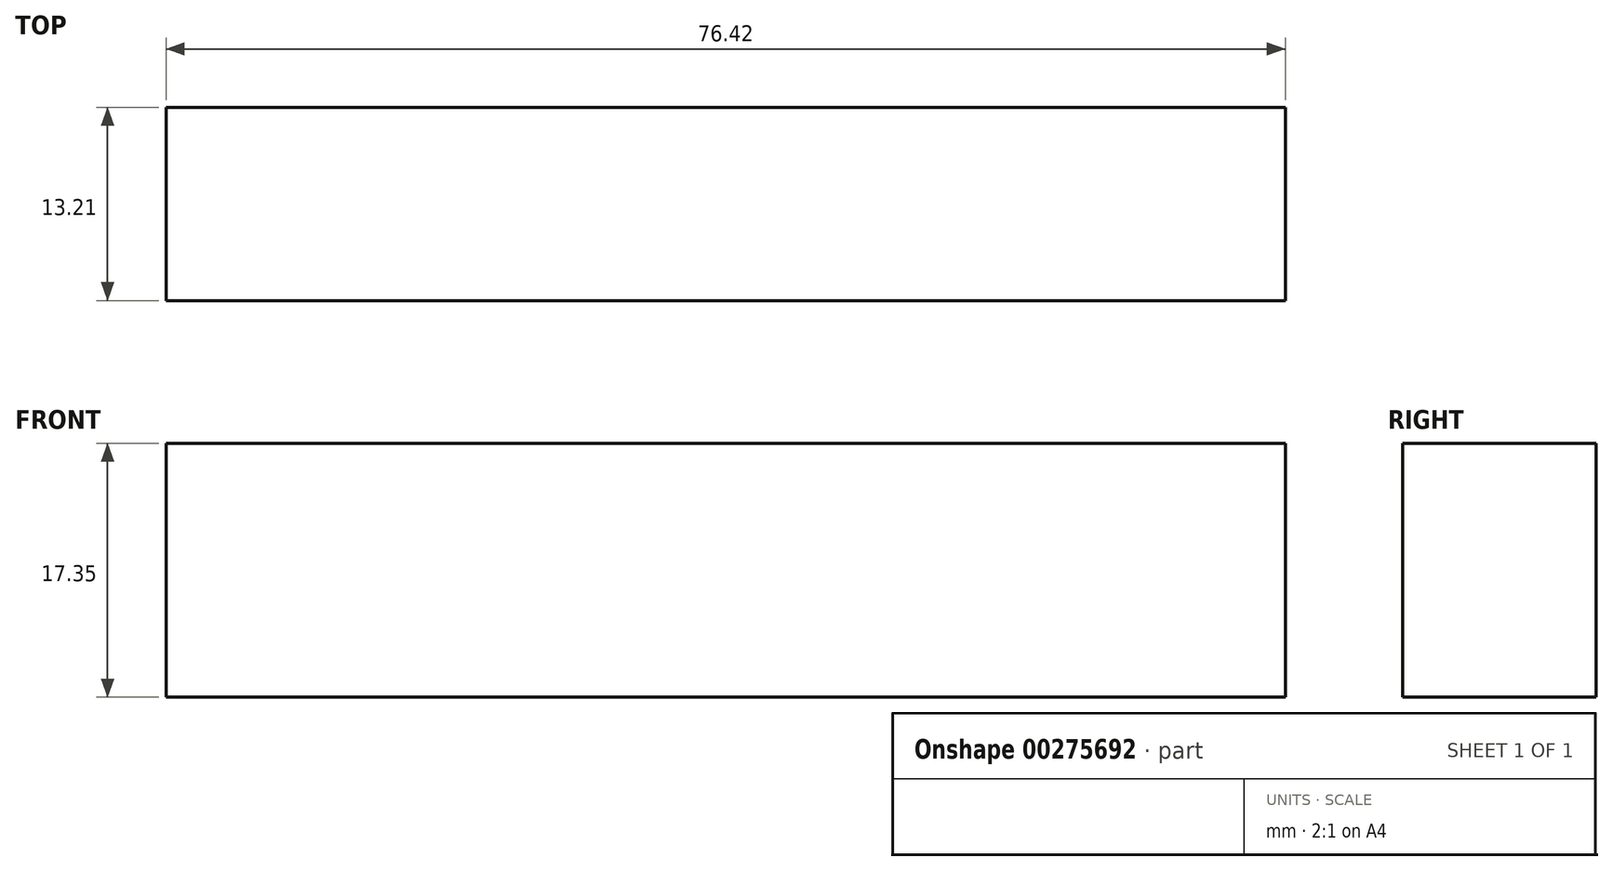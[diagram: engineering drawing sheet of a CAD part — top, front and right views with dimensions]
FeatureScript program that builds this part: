
annotation { "Feature Type Name" : "Feature", "Feature Type Description" : "" }
export const myFeature = defineFeature(function(context is Context, id is Id, definition is map)
    precondition{}
    {
        {
            var Q0;
            Q0=qCreatedBy(makeId("Front.planeOp"),FACE);
            var sketch = newSketch(context, id + "F0", { "sketchPlane" : qUnion([Q0])});
            skLineSegment(sketch, "E0.bottom", {"start": v(18.77, 17.35) * mm, "end": v(95.19, 17.35) * mm});
            skLineSegment(sketch, "E0.top", {"start": v(18.77, 0) * mm, "end": v(95.19, 0) * mm});
            skLineSegment(sketch, "E0.left", {"start": v(18.77, 17.35) * mm, "end": v(18.77, 0) * mm});
            skLineSegment(sketch, "E0.right", {"start": v(95.19, 17.35) * mm, "end": v(95.19, 0) * mm});
            skSolve(sketch);
        }
        {
            var Q0;
            Q0=makeQuery(id+"F0.imprint","IMPRINT",FACE,{"disambiguationData":[TD([[makeQuery(id+"F0.imprint","IMPRINT",EDGE,{"derivedFrom":sQuery(id+"F0.wireOp",EDGE,"E0.bottom")}),-1.0]])]});
            extrude(context, id + "F1", {"entities" : qUnion([Q0]), "depth" : 13.2 * mm});
        }
    });
